# Revit family: QF_Woodson_Module Square Hot Food Display_W.HFSQ22_W.HFSQ26
name_source: partatom
category: Specialty Equipment
revit_build: Autodesk Revit MEP 2014 (Build: 20140709_2115(x64)
units: mm (PartAtom-declared; Revit-internal decimal feet)

## types (5) — shared parameters
Assembly Code = E1090300
Body = QF_Stainless-Polished
Depth = 600 mm  [stored 1.9685 ft]
Drain Connector = 20 mm  [stored 0.0656168 ft]
Glass = QF_Glass
Handle = QF_Plastic-Black-Coarse
Height = 702 mm  [stored 2.30315 ft]
Leg = QF_Plastic-Black-Coarse
Leg Height = 32 mm  [stored 0.104987 ft]
Manufacturer = Woodson
Switch = QF_Plastic-Black-Coarse
Type Comments = The Woodson square profile hot food display combines market leading features and aesthetically pleasing modern styling
URL = http://www.stoddart.com.au
Volts = 240 V

## per-type parameters (varying)
| type | Description | FL Amps | Half Width | Middle Leg | Multi Grill | Number of Grill | Single Grill | Watts | Weight | Width |
| W.HFSQ26 | Square Profile Hot Food Display,6 module unit | 15 A | 1003 mm | Yes | Yes | 5 | No | 3300 W | 78.00 kg | 2005 mm  [stored 6.57808 ft] |
| W.HFSQ25 | Square Profile Hot Food Display,5 module unit | 15 A | 840 mm  [stored 2.75591 ft] | Yes | Yes | 4 | No | 3300 W | 68.00 kg | 1680 mm  [stored 5.51181 ft] |
| W.HFSQ24 | Square Profile Hot Food Display,4 module unit | 15 A | 678 mm | Yes | Yes | 3 | No | 3000 W | 58.00 kg | 1355 mm  [stored 4.44554 ft] |
| W.HFSQ23 | Square Profile Hot Food Display,3 module unit | 10 A | 515 mm  [stored 1.68963 ft] | No | Yes | 2 | No | 2400 W | 48.00 kg | 1030 mm  [stored 3.37927 ft] |
| W.HFSQ22 | Square Profile Hot Food Display,2 module unit | 10 A | 353 mm | No | No | 2 | Yes | 1500 W | 38.00 kg | 705 mm  [stored 2.31299 ft] |

note: column(s) folded — value = type name in every type: Model

note: [stored X ft] marks values corroborated as IEEE doubles in the binary element streams (Revit-internal decimal feet)

## geometry (parser evidence)
native form markers: Sweep x2
no freeform markers — native parametric forms only
